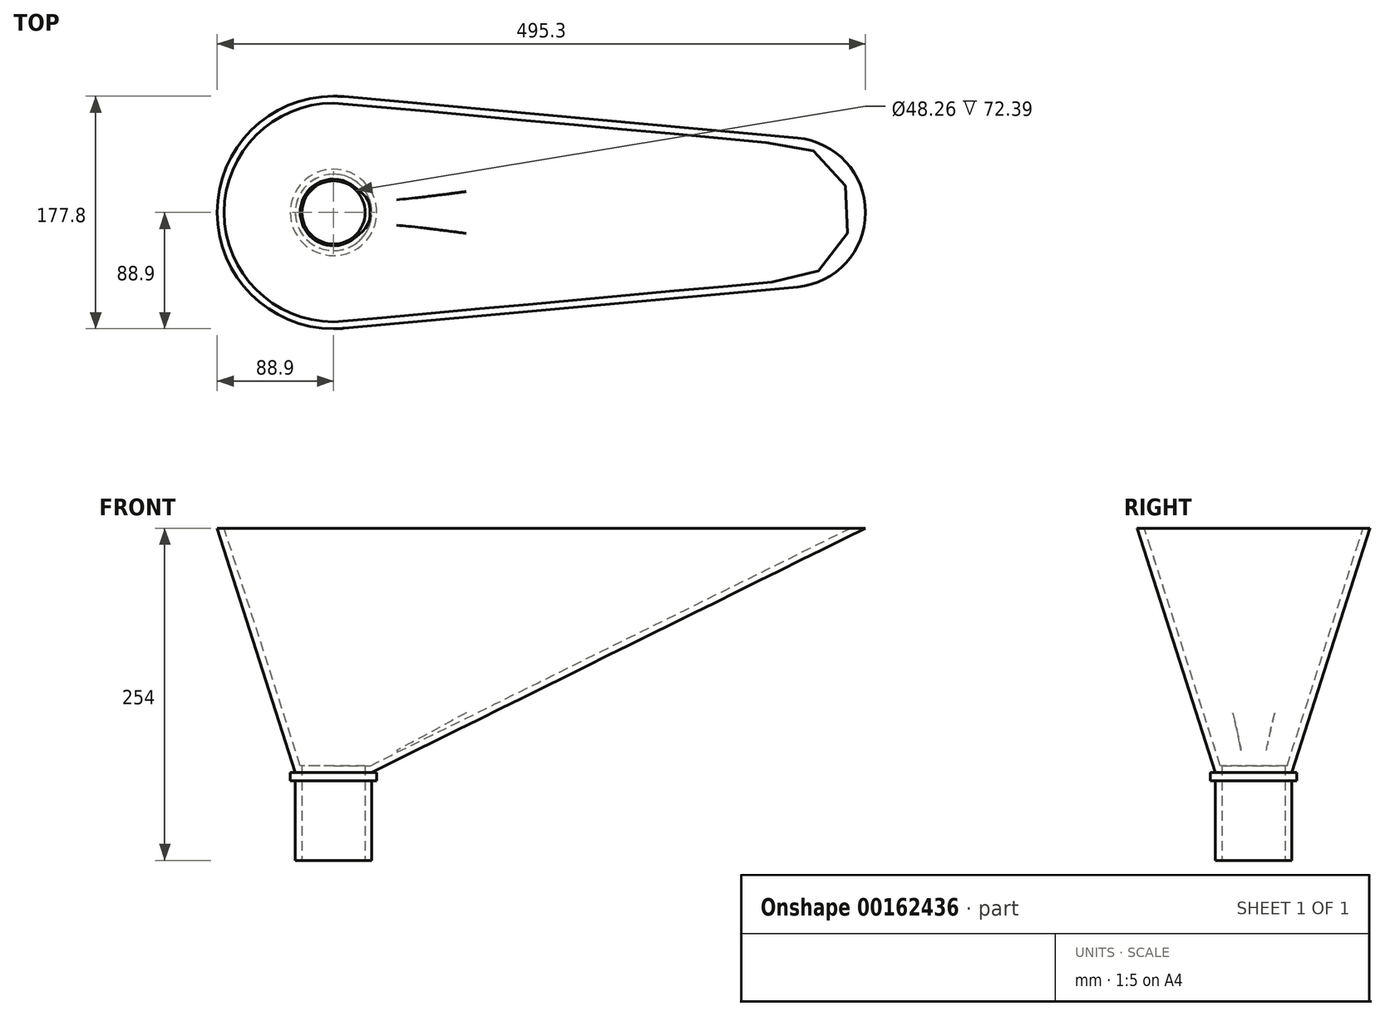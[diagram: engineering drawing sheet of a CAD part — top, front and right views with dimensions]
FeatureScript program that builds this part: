
annotation { "Feature Type Name" : "Feature", "Feature Type Description" : "" }
export const myFeature = defineFeature(function(context is Context, id is Id, definition is map)
    precondition{}
    {
        {
            var Q0;
            Q0=qCreatedBy(makeId("Top.planeOp"),FACE);
            var sketch = newSketch(context, id + "F0", { "sketchPlane" : qUnion([Q0])});
            skCircle(sketch, "E0", {"center": v(0, 0) * mm, "radius": 29.21 * mm});
            skCircle(sketch, "E1.0", {"center": v(0, 0) * mm, "radius": 24.13 * mm});
            skSolve(sketch);
        }
        {
            var Q0;
            Q0 = qSketchRegion(id + "F0", true);
            extrude(context, id + "F1", {"entities" : qUnion([Q0]), "depth" : 60.96 * mm, "hasSecondDirection" : true, "secondDirectionOppositeDirection" : true, "secondDirectionDepth" : 6.35 * mm});
        }
        {
            var Q0;
            Q0=qCreatedBy(makeId("Top.planeOp"),FACE);
            cPlane(context, id + "F2", {"entities" : qUnion([Q0]), "cplaneType" : CPlaneType.OFFSET, "offset" : 247.65 * mm, "width" : 152.4 * mm, "height" : 152.4 * mm});
        }
        {
            var Q0;
            Q0=qCreatedBy(id+"F2.planeOp",FACE);
            var sketch = newSketch(context, id + "F3", { "sketchPlane" : qUnion([Q0])});
            skCircle(sketch, "E2", {"center": v(0, 0) * mm, "radius": 88.9 * mm});
            skCircle(sketch, "E3", {"center": v(349.25, 0) * mm, "radius": 57.15 * mm});
            skLineSegment(sketch, "E4", {"start": v(8.08, -88.53) * mm, "end": v(354.45, -56.91) * mm});
            skLineSegment(sketch, "E5", {"start": v(354.45, 56.91) * mm, "end": v(8.08, 88.53) * mm});
            skSolve(sketch);
        }
        {
            var Q0;
            Q0=makeQuery(id+"F1.opExtrude","CAP_FACE",FACE,{"disambiguationData":[OSD([sQuery(id+"F0.wireOp",EDGE,"E0"),sQuery(id+"F0.wireOp",EDGE,"E1.0")])],"isStart":false});
            var sketch = newSketch(context, id + "F4", { "sketchPlane" : qUnion([Q0])});
            skCircle(sketch, "E6.0", {"center": v(0, 0) * mm, "radius": 29.21 * mm});
            skSolve(sketch);
        }
        {
            var Q0;
            Q0=qCreatedBy(makeId("Right.planeOp"),FACE);
            var sketch = newSketch(context, id + "F5", { "sketchPlane" : qUnion([Q0])});
            skLineSegment(sketch, "E7.0", {"start": v(-29.21, 60.96) * mm, "end": v(29.21, 60.96) * mm, "construction": true});
            skLineSegment(sketch, "E8.0", {"start": v(-88.9, 247.65) * mm, "end": v(88.9, 247.65) * mm});
            skLineSegment(sketch, "E9", {"start": v(29.21, 60.96) * mm, "end": v(88.9, 247.65) * mm});
            skLineSegment(sketch, "E10", {"start": v(-29.21, 60.96) * mm, "end": v(-88.9, 247.65) * mm});
            skSolve(sketch);
        }
        {
            var Q1;
            Q1 = qSketchRegion(id + "F4", true);
            var Q2;
            Q2 = qSketchRegion(id + "F3", true);
            var Q3;
            Q3=sQuery(id+"F5.wireOp",EDGE,"E9");
            var Q4;
            Q4=sQuery(id+"F5.wireOp",EDGE,"E10");
            loft(context, id + "F6", {"operationType" : NewBodyOperationType.ADD, "addGuides" : true, "sheetProfilesArray" : [{ "sheetProfileEntities" : qUnion([Q1]) }, { "sheetProfileEntities" : qUnion([Q2]) }], "guidesArray" : [{ "guideEntities" : qUnion([Q3]), "guideDerivativeType" : LoftGuideDerivativeType.DEFAULT, "guideDerivativeMagnitude" : 1 }, { "guideEntities" : qUnion([Q4]), "guideDerivativeType" : LoftGuideDerivativeType.DEFAULT, "guideDerivativeMagnitude" : 1 }]});
        }
        {
            var Q0;
            {var subQ0=sQuery(id+"F3.wireOp",EDGE,"E4");Q0=makeQuery(id+"F6.opLoft","CAP_FACE",FACE,{"disambiguationData":[OSD([makeQuery(id+"F3.imprint","IMPRINT",FACE,{"disambiguationData":[TD([[makeQuery(id+"F3.imprint","IMPRINT",EDGE,{"derivedFrom":subQ0}),1.0]])]})])],"isStart":true});}
            shell(context, id + "F7", {"entities" : qUnion([Q0]), "thickness" : 5.08 * mm});
        }
        {
            var Q0;
            Q0=makeQuery(id+"F6.opLoft","CAP_FACE",FACE,{"disambiguationData":[OSD([makeQuery(id+"F4.imprint","IMPRINT",FACE,{"disambiguationData":[TD([[makeQuery(id+"F4.imprint","IMPRINT",EDGE,{"derivedFrom":makeQuery(id+"F1.opExtrude","CAP_EDGE",EDGE,{"disambiguationData":[OSD([sQuery(id+"F0.wireOp",EDGE,"E1.0")])],"isStart":false})}),1.0]])]})])],"isStart":true});
            var sketch = newSketch(context, id + "F8", { "sketchPlane" : qUnion([Q0])});
            skCircle(sketch, "E11.0", {"center": v(0, 0) * mm, "radius": 24.13 * mm});
            skSolve(sketch);
        }
        {
            var Q0;
            Q0 = qSketchRegion(id + "F8", true);
            extrude(context, id + "F9", {"entities" : qUnion([Q0]), "operationType" : NewBodyOperationType.REMOVE, "endBound" : BoundingType.THROUGH_ALL, "oppositeDirection" : true, "depth" : 25.4 * mm});
        }
        {
            var Q0;
            Q0=makeQuery(id+"F1.opExtrude","CAP_FACE",FACE,{"disambiguationData":[OSD([sQuery(id+"F0.wireOp",EDGE,"E0"),sQuery(id+"F0.wireOp",EDGE,"E1.0")])],"isStart":true});
            cPlane(context, id + "F10", {"entities" : qUnion([Q0]), "cplaneType" : CPlaneType.OFFSET, "offset" : 67.3 * mm, "oppositeDirection" : true, "width" : 152.4 * mm, "height" : 152.4 * mm});
        }
        {
            var Q0;
            Q0=qCreatedBy(id+"F10.planeOp",FACE);
            var sketch = newSketch(context, id + "F11", { "sketchPlane" : qUnion([Q0])});
            skPoint(sketch, "E12.0", {"position": v(0, 0) * mm});
            skCircle(sketch, "E13", {"center": v(0, 0) * mm, "radius": 33.02 * mm});
            skCircle(sketch, "E14.0", {"center": v(0, 0) * mm, "radius": 24.13 * mm});
            skSolve(sketch);
        }
        {
            var Q0;
            Q0 = qSketchRegion(id + "F11", true);
            extrude(context, id + "F12", {"entities" : qUnion([Q0]), "operationType" : NewBodyOperationType.ADD, "depth" : 6.35 * mm});
        }
    });
